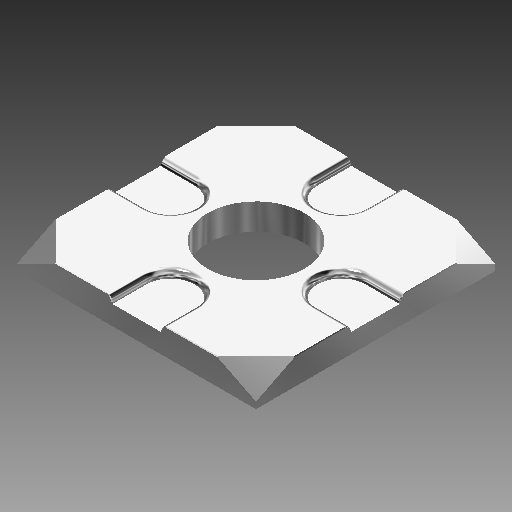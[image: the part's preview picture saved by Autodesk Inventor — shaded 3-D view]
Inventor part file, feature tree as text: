
AUTODESK INVENTOR PART (.ipt)
format: ipt  version: 2019 (Build 230136000, 136)  size: 223,232 bytes
history: native  units: in
note: dims shown in document units (in); Inventor stores cm internally (conversion verified against a paired STEP export)
features: extrude x3, sketch x3, chamfer x2, fillet x1
ambient origin geometry x8: Origin, YZ Plane, XZ Plane, XY Plane, X Axis, Y Axis, Z Axis, Center Point
bodies: Solid1 (feature_tree)
feature tree (9):
  extrude  "Extrusion1"  Depth=0.383in
  extrude  "Extrusion2"  Depth=0.042in
  fillet  "Fillet1"  Radius=0.077in
  extrude  "Extrusion3"  Depth=0.011in
  chamfer  "Chamfer1"  Distance=0.0385in
  chamfer  "Chamfer2"  Distance=0.093in
  sketch  "Sketch1"  dims[d0=0.383in d1=0.383in]
  sketch  "Sketch2"  dims[d2=0.042in d3=0.0in d10=0.0385in d11=0.077in]
  sketch  "Sketch3"  dims[d12=0.093in d13=0.093in d14=0.0385in d15=0.093in d16=0.0385in d17=0.093in d18=0.0385in d19=0.011in d20=0.0in d21=0.011in d22=0.155in d23=0.011in d24=0.0in d25=0.001in d26=0.125in d27=45.0deg d28=0.05in d29=0.125in d30=45.0deg]
